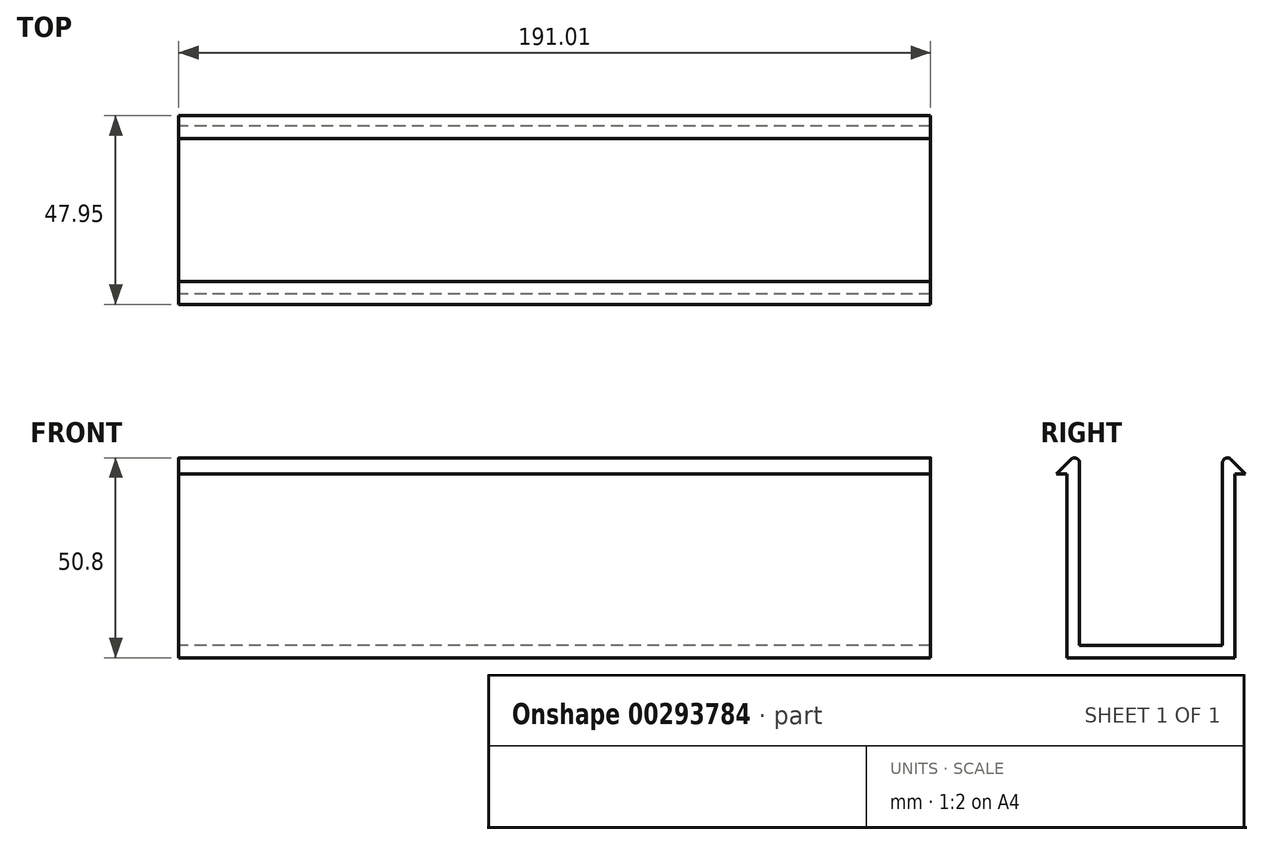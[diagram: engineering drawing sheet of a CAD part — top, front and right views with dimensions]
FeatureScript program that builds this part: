
annotation { "Feature Type Name" : "Feature", "Feature Type Description" : "" }
export const myFeature = defineFeature(function(context is Context, id is Id, definition is map)
    precondition{}
    {
        {
            var Q0;
            Q0=qCreatedBy(makeId("Right.planeOp"),FACE);
            var sketch = newSketch(context, id + "F0", { "sketchPlane" : qUnion([Q0])});
            skLineSegment(sketch, "E0", {"start": v(0, 0) * mm, "end": v(42.67, 0) * mm});
            skLineSegment(sketch, "E1", {"start": v(39.5, 3.18) * mm, "end": v(39.5, 49.53) * mm});
            skLineSegment(sketch, "E2", {"start": v(39.5, 3.18) * mm, "end": v(3.18, 3.18) * mm});
            skLineSegment(sketch, "E3", {"start": v(3.18, 3.17) * mm, "end": v(3.18, 49.53) * mm});
            skLineSegment(sketch, "E4", {"start": v(42.67, 0) * mm, "end": v(42.67, 46.78) * mm});
            skLineSegment(sketch, "E5", {"start": v(0, 0) * mm, "end": v(0, 46.78) * mm});
            skArc(sketch, "E6", {"start": v(39.5, 49.53) * mm, "mid": v(40.28, 50.7) * mm, "end": v(41.67, 50.43) * mm});
            skArc(sketch, "E7", {"start": v(3.18, 49.53) * mm, "mid": v(2.4, 50.7) * mm, "end": v(1, 50.43) * mm});
            skLineSegment(sketch, "E8", {"start": v(42.67, 46.78) * mm, "end": v(45.31, 46.78) * mm});
            skLineSegment(sketch, "E9", {"start": v(0, 46.78) * mm, "end": v(-2.64, 46.78) * mm});
            skLineSegment(sketch, "E10", {"start": v(41.67, 50.43) * mm, "end": v(45.31, 46.78) * mm});
            skLineSegment(sketch, "E11", {"start": v(1, 50.43) * mm, "end": v(-2.64, 46.78) * mm});
            skLineSegment(sketch, "E12", {"start": v(39.5, 12.95) * mm, "end": v(42.67, 12.95) * mm});
            skLineSegment(sketch, "E13", {"start": v(39.5, 44.45) * mm, "end": v(42.67, 44.45) * mm});
            skLineSegment(sketch, "E14", {"start": v(3.18, 44.45) * mm, "end": v(0, 44.45) * mm});
            skLineSegment(sketch, "E15", {"start": v(0, 12.95) * mm, "end": v(3.18, 12.95) * mm});
            skSolve(sketch);
        }
        {
            var Q0;
            Q0 = qSketchRegion(id + "F0", true);
            extrude(context, id + "F1", {"entities" : qUnion([Q0]), "depth" : 191 * mm});
        }
    });
